# Revit family: Boiler-Gas-Weil-McLain-SVF_1000
name_source: partatom
category: Mechanical Equipment
units: mm (PartAtom-declared; Revit-internal decimal feet)

## family parameters
Always vertical = Yes
Cut with Voids When Loaded = No
OmniClass Number = 23.75.10.11.14
OmniClass Title = Hot Water Heat Generators
Part Type = Normal
Room Calculation Point = No
Round Connector Dimension = Use Diameter
Shared = No
Work Plane-Based = Yes

## types (1)
- SVF1000
    Assembly Code = D3020100
    Boiler Return Water Diameter = 3"
    Boiler Supply Water Diameter = 3"
    Condensate Drain Connection Diameter = 1"
    CondensateCL = 0' - 4"
    Dead Weight = 1750
    Default Elevation = 0' - 0"
    Description = Weil-McLain Commercial NG Gas Boiler - SVF1000 Boiler as Specified
    Flue Diameter = 6"
    FlueHolderDia = 0' - 7 1/2"
    Frame Accent Material = Plastic - WeilMcLain - Black
    Frame Finish = Metal - WeilMcLain - Gray
    Frequency = 60 Hz
    Fuel Type = Natural Gas
    Full Load Current = 23 A
    Gas Connection Diameter = 1"
    Gas Connection Type = Female NPT
    Height = 6' - 6 3/16"
    Keynote = 23 52 00
    Length = 4' - 8 5/16"
    Manufacturer = Weil-McLain
    Model = SVF1000
    Net AHRI MBH = 1259.0 Btu/h
    Number of Poles = 1
    Operating Temperature = 40 - 120 F
    Operating Weight = 2000
    Phase = 1
    Product Name = SVF1000 Boiler
    Product Page URL = https://www.weil-mclain.com
    Screen Material = Plastic - WeilMcLain - Blue
    Standards Conformance = ASME  ;  AHRI  ;  CSA
    Supply Air Connection Diameter = 6"
    Tank Capacity = 118 gal
    Thermal Efficiency = 96.5
    Total Heating Capacity = 1448.0 Btu/h
    Type Comments = No Side Clearance. Side-by-Side install capable.
    URL = https://www.weil-mclain.com
    Voltage = 120 V
    Water Connection Type = Class 150 ASME Flange
    Width = 2' - 11 3/16"

## geometry (parser evidence)
native form markers: Sweep x2
no freeform markers — native parametric forms only
